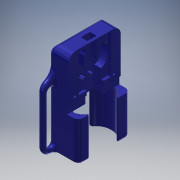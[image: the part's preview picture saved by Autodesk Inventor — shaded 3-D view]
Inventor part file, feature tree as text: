
AUTODESK INVENTOR PART (.ipt)
format: ipt  version: 2018 (Build 220112000, 112)  size: 927,232 bytes
history: native  units: in
note: dims shown in document units (in); Inventor stores cm internally (conversion verified against a paired STEP export)
features: move_body x21, extrude x15, sketch x13, direct_edit x9, fillet x9, thicken_offset x1
ambient origin geometry x8: Origin, YZ Plane, XZ Plane, XY Plane, X Axis, Y Axis, Z Axis, Center Point
bodies: Solid1 (feature_tree)
feature tree (68):
  sketch  "Sketch1"  dims[d4=0.4724in d5=0.2362in]
  extrude  "Extrusion1"  Depth=0.2362in
  extrude  "Extrusion2"  Depth=0.3543in
  extrude  "Extrusion3"  Depth=0.3346in
  thicken_offset  "Thicken1"
  extrude  "Extrusion4"  Depth=0.4724in
  extrude  "Extrusion5"  Depth=0.0394in
  direct_edit  "Direct Edit1"
  direct_edit  "Direct Edit2"
  extrude  "Extrusion6"  Depth=0.3937in
  extrude  "Extrusion7"  Depth=0.1969in
  direct_edit  "Direct Edit3"
  direct_edit  "Direct Edit4"
  sketch  "Sketch6"  dims[d14=0.3937in d15=0.3937in]
  extrude  "Extrusion8"  Depth=0.1969in
  extrude  "Extrusion9"  Depth=0.6693in TaperAngle=0.0deg
  extrude  "Extrusion10"  Depth=0.0394in
  direct_edit  "Direct Edit5"
  direct_edit  "Direct Edit6"
  extrude  "Extrusion11"  Depth=0.1575in
  fillet  "Fillet4"  Radius=0.1181in
  extrude  "Extrusion12"  Depth=0.1181in TaperAngle=0.0deg
  direct_edit  "Direct Edit7"
  direct_edit  "Direct Edit10"
  extrude  "Extrusion13"  TaperAngle=90.0deg  [1 undecoded]
  sketch  "Sketch11"  dims[d28=0.0787in d29=0.1575in d30=0.1181in]
  extrude  "Extrusion14"  Depth=0.3543in
  fillet  "Fillet21"  Radius=1.9685in
  fillet  "Fillet22"  [1 undecoded]
  fillet  "Fillet23"  Radius=0.3543in
  fillet  "Fillet24"  Radius=0.7874in
  fillet  "Fillet25"  Radius=0.1575in
  fillet  "Fillet26"  Radius=0.1969in
  fillet  "Fillet27"  Radius=0.315in
  extrude  "Extrusion15"  Depth=0.315in
  sketch  "Sketch14"  dims[d34=3.937in d35=90.0deg d36=0.3543in d37=1.9685in d39=0.0in d40=0.3543in d41=0.7874in d42=0.1575in d43=0.1969in d44=0.315in d45=0.315in d46=0.1575in d47=0.0in d54=0.0in d55=0.0in d56=-0.0787in d57=0.0in d58=0.0in d59=-0.0197in d60=0.0in d61=0.0in d62=-0.0197in d63=0.2756in d64=1.5748in d65=0.1181in d66=0.0in d68=1.378in d69=0.0in d70=0.0in d71=0.03in d72=0.03in d73=0.2362in d79=0.0787in d80=90.0deg d82=0.6476in d83=0.6476in d84=0.9206in d85=0.9206in d86=0.315in d87=0.1407in d88=0.0787in d89=0.0in d92=0.0in d93=0.0in d94=-0.0197in d95=0.0in d96=0.0in d97=-0.0197in d98=0.0in d99=0.0in d100=-0.0197in d101=0.0in d102=0.0in d103=-0.0197in d104=0.0in d105=0.0in d106=-0.0591in d107=0.0in d108=0.0in d109=-0.0591in d110=1.5748in d111=0.2362in d112=0.0in d113=0.0in d114=0.1575in d115=0.0in d116=0.1969in d117=0.0in d118=0.0in d119=0.0in d120=-0.1181in d121=0.0in d122=0.0in d123=-0.1181in d124=0.0in d125=0.0in d126=-0.1181in d127=0.0787in d128=0.1969in d129=0.1969in d130=0.3937in d131=0.0in d132=0.0in d133=0.1181in d149=0.3937in d150=0.0in d151=0.0in d152=0.0in d153=-0.0787in d160=0.0in d161=0.0in d162=-0.0079in d163=1.5748in d165=0.0197in d166=0.0197in d167=7.874in d168=0.0in d170=0.1969in d171=1.5748in d173=0.1575in d174=0.1575in d175=0.1575in d176=0.1575in d177=0.7874in d178=90.0deg d179=0.1575in d180=0.0in d192=0.0in d193=0.0984in d194=0.3543in d195=0.0984in d196=0.2559in d197=0.0787in d198=0.0197in d199=0.1575in d200=0.0787in d201=0.0787in d202=0.0394in d203=0.2362in d204=0.0in d205=0.0in d206=-0.0118in d207=0.3543in d208=0.1575in d209=0.0in d210=0.0in d211=0.0in d212=0.121in d213=0.0in d214=0.0in d215=0.1637in d216=0.0in d217=0.0in d218=0.0787in d219=0.0in d220=0.0in d221=0.0787in d222=0.0in d223=0.0in d224=-0.0394in d225=0.0in d226=0.0in d227=-0.0394in d228=0.0394in]
  direct_edit  "Direct Edit11"
  fillet  "Fillet28"  Radius=0.1575in
  sketch  "Sketch2"  dims[d6=0.2362in d7=0.3543in]
  sketch  "Sketch3"  dims[d8=0.374in d9=0.3346in]
  sketch  "Sketch4"  dims[d10=0.4724in d11=0.4724in]
  sketch  "Sketch5"  dims[d12=0.3543in d13=0.0394in]
  sketch  "Sketch7"  dims[d16=0.1969in d17=0.1969in]
  sketch  "Sketch8"  dims[d18=0.1969in d19=0.1969in]
  sketch  "Sketch9"  dims[d20=1.5748in d21=0.0in d22=0.6693in d23=0.0in]
  sketch  "Sketch10"  dims[d24=1.1811in d25=0.0in d26=0.0394in d27=0.0394in]
  sketch  "Sketch13"  dims[d31=0.1181in d32=0.1181in d33=0.0in]
  move_body  "Move1"
  move_body  "Move2"
  move_body  "Move3"
  move_body  "Move4"
  move_body  "Move5"
  move_body  "Move6"
  move_body  "Move7"
  move_body  "Move8"
  move_body  "Move9"
  move_body  "Move10"
  move_body  "Move11"
  move_body  "Move12"
  move_body  "Move13"
  move_body  "Move16"
  move_body  "Move17"
  move_body  "Move18"
  move_body  "Move19"
  move_body  "Move20"
  move_body  "Move21"
  move_body  "Move22"
  move_body  "Move23"
note: 2 required parameter values undecoded (feature->parameter linkage not recoverable at this tier; creation-order binding heuristic only, values carry confidence <= 0.55)
